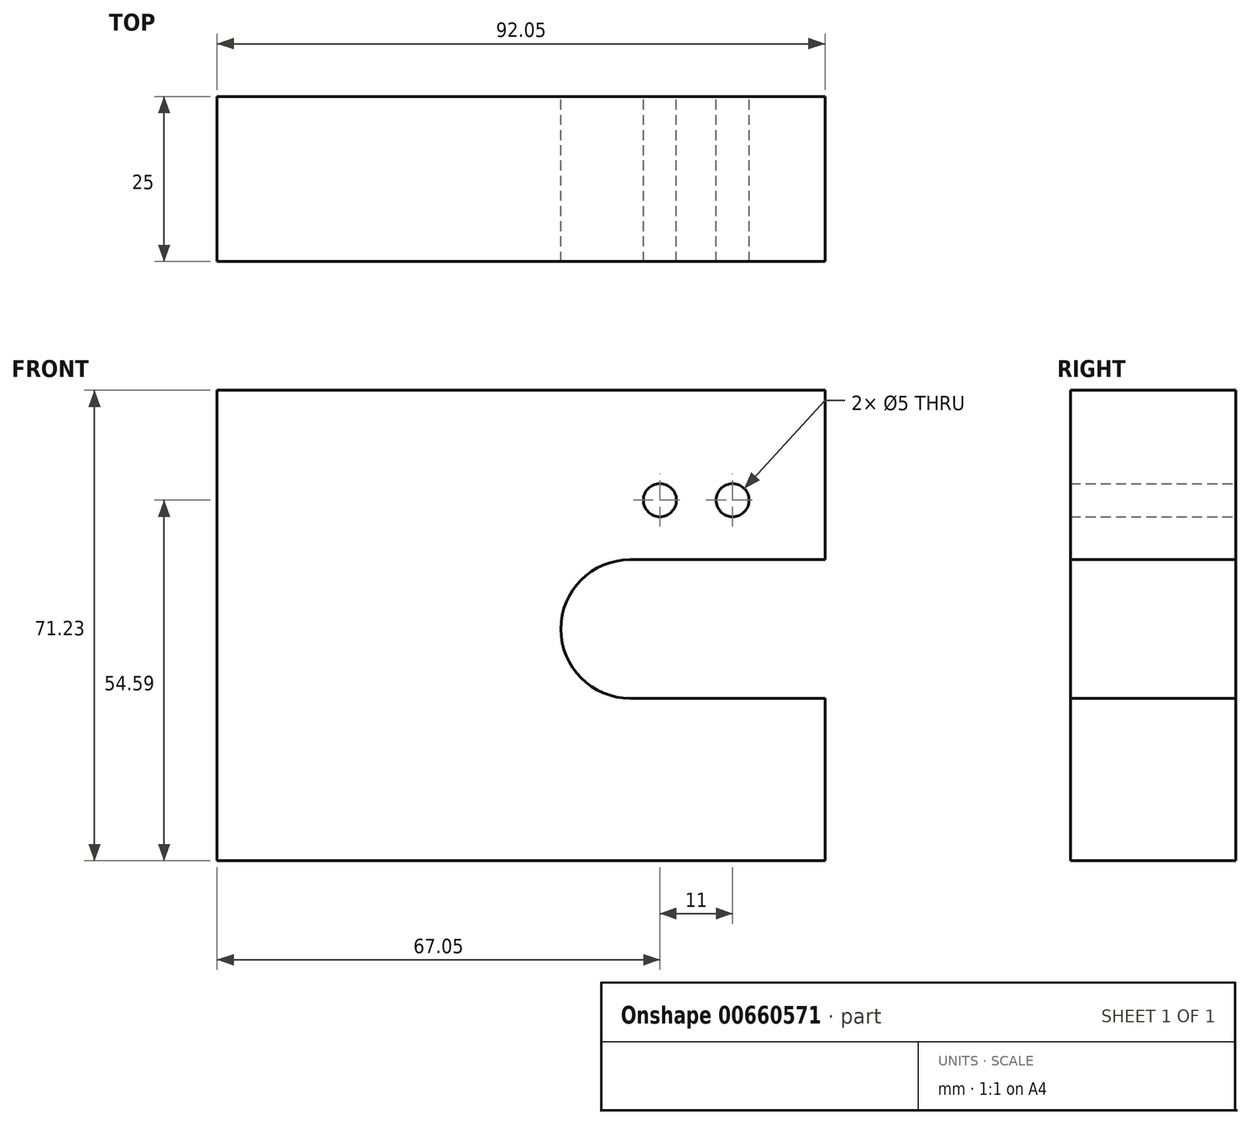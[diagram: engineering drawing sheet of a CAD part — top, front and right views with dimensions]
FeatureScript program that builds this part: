
annotation { "Feature Type Name" : "Feature", "Feature Type Description" : "" }
export const myFeature = defineFeature(function(context is Context, id is Id, definition is map)
    precondition{}
    {
        {
            var Q0;
            Q0=qCreatedBy(makeId("Front.planeOp"),FACE);
            var sketch = newSketch(context, id + "F0", { "sketchPlane" : qUnion([Q0])});
            skArc(sketch, "E0", {"start": v(0, 10.5) * mm, "mid": v(-10.5, 0) * mm, "end": v(0, -10.5) * mm});
            skLineSegment(sketch, "E1.bottom", {"start": v(29.5, 36.14) * mm, "end": v(-62.55, 36.14) * mm});
            skLineSegment(sketch, "E1.top", {"start": v(29.5, -35.09) * mm, "end": v(-62.55, -35.09) * mm});
            skLineSegment(sketch, "E1.left", {"start": v(29.5, 36.14) * mm, "end": v(29.5, 10.5) * mm});
            skLineSegment(sketch, "E1.right", {"start": v(-62.55, 36.14) * mm, "end": v(-62.55, -35.09) * mm});
            skLineSegment(sketch, "E2", {"start": v(0, 10.5) * mm, "end": v(29.5, 10.5) * mm});
            skLineSegment(sketch, "E3", {"start": v(29.5, 10.5) * mm, "end": v(29.25, 11.3) * mm});
            skLineSegment(sketch, "E4", {"start": v(0, -10.5) * mm, "end": v(29.5, -10.5) * mm});
            skLineSegment(sketch, "E5.trimOffspring", {"start": v(29.5, -10.5) * mm, "end": v(29.5, -35.09) * mm});
            skCircle(sketch, "E6", {"center": v(15.5, 19.5) * mm, "radius": 2.5 * mm});
            skCircle(sketch, "E7", {"center": v(4.5, 19.5) * mm, "radius": 2.5 * mm});
            skSolve(sketch);
        }
        {
            var Q0;
            Q0=makeQuery(id+"F0.imprint","IMPRINT",FACE,{"disambiguationData":[TD([[makeQuery(id+"F0.imprint","IMPRINT",EDGE,{"derivedFrom":sQuery(id+"F0.wireOp",EDGE,"E0")}),-1.0]])]});
            extrude(context, id + "F1", {"entities" : qUnion([Q0]), "depth" : 25 * mm, "offsetDistance" : 25 * mm});
        }
    });
